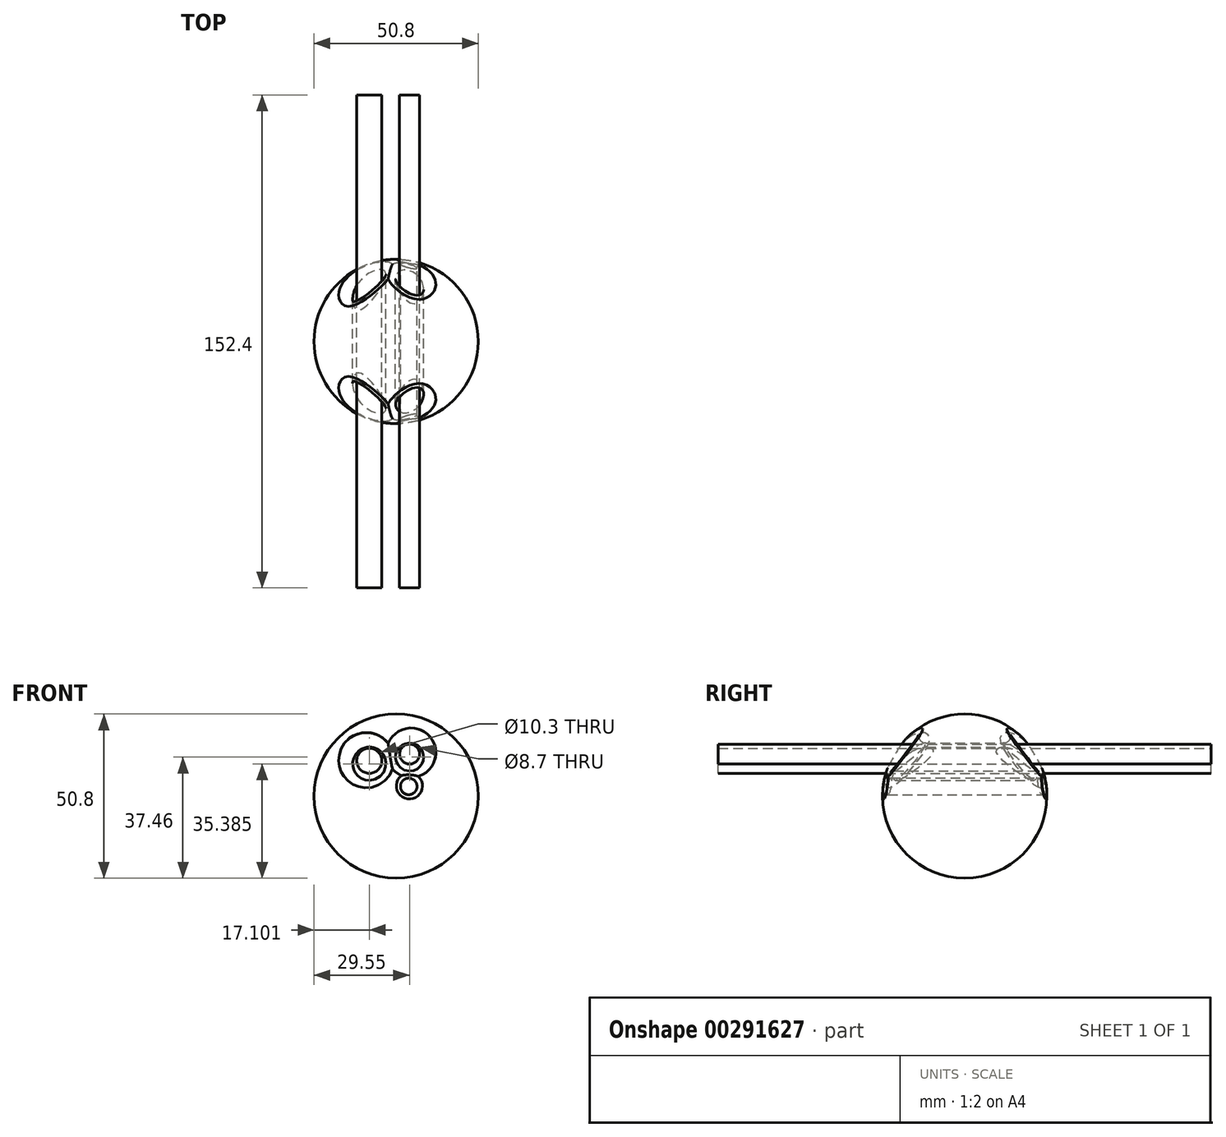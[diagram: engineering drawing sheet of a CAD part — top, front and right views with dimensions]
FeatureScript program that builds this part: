
annotation { "Feature Type Name" : "Feature", "Feature Type Description" : "" }
export const myFeature = defineFeature(function(context is Context, id is Id, definition is map)
    precondition{}
    {
        {
            var Q0;
            Q0=qCreatedBy(makeId("Front.planeOp"),FACE);
            var sketch = newSketch(context, id + "F0", { "sketchPlane" : qUnion([Q0])});
            skCircle(sketch, "E0", {"center": v(0, 0) * mm, "radius": 25.4 * mm});
            skCircle(sketch, "E1", {"center": v(-8.3, 9.99) * mm, "radius": 5.15 * mm});
            skCircle(sketch, "E2", {"center": v(4.15, 12.06) * mm, "radius": 4.35 * mm});
            skCircle(sketch, "E3", {"center": v(3.9, 2.98) * mm, "radius": 2.57 * mm});
            skCircle(sketch, "E4", {"center": v(-8.3, 10.92) * mm, "radius": 3.9 * mm});
            skCircle(sketch, "E5", {"center": v(4.15, 13) * mm, "radius": 3.08 * mm});
            skSolve(sketch);
        }
        {
            var Q0;
            Q0=makeQuery(id+"F0.imprint","IMPRINT",FACE,{"disambiguationData":[TD([[makeQuery(id+"F0.imprint","IMPRINT",EDGE,{"derivedFrom":sQuery(id+"F0.wireOp",EDGE,"E0")}),1.0]])]});
            extrude(context, id + "F1", {"entities" : qUnion([Q0]), "endBound" : BoundingType.SYMMETRIC, "depth" : 50.8 * mm});
        }
        {
            var Q0;
            Q0=makeQuery(id+"F1.opExtrude","CAP_EDGE",EDGE,{"disambiguationData":[OSD([sQuery(id+"F0.wireOp",EDGE,"E0")])],"isStart":false});
            fillet(context, id + "F2", {"entities" : qUnion([Q0]), "radius" : 25.4 * mm, "tangentPropagation" : true, "allowEdgeOverflow" : false});
        }
        {
            var Q0;
            Q0=makeQuery(id+"F1.opExtrude","CAP_EDGE",EDGE,{"disambiguationData":[OSD([sQuery(id+"F0.wireOp",EDGE,"E0")])],"isStart":true});
            fillet(context, id + "F3", {"entities" : qUnion([Q0]), "radius" : 25.4 * mm, "tangentPropagation" : true, "allowEdgeOverflow" : false});
        }
        {
            var Q0;
            Q0=makeQuery(id+"F1.opExtrude","SWEPT_FACE",FACE,{"disambiguationData":[OSD([sQuery(id+"F0.wireOp",EDGE,"E2")])]});
            fillet(context, id + "F4", {"entities" : qUnion([Q0]), "radius" : 2.54 * mm, "tangentPropagation" : true, "allowEdgeOverflow" : false});
        }
        {
            var Q0;
            Q0=makeQuery(id+"F1.opExtrude","SWEPT_FACE",FACE,{"disambiguationData":[OSD([sQuery(id+"F0.wireOp",EDGE,"E1")])]});
            fillet(context, id + "F5", {"entities" : qUnion([Q0]), "radius" : 2.54 * mm, "tangentPropagation" : true, "allowEdgeOverflow" : false});
        }
        {
            var Q0;
            Q0=makeQuery(id+"F1.opExtrude","SWEPT_FACE",FACE,{"disambiguationData":[OSD([sQuery(id+"F0.wireOp",EDGE,"E3")])]});
            fillet(context, id + "F6", {"entities" : qUnion([Q0]), "radius" : 1.27 * mm, "tangentPropagation" : true, "allowEdgeOverflow" : false});
        }
        {
            var Q0;
            Q0=makeQuery(id+"F0.imprint","IMPRINT",FACE,{"disambiguationData":[TD([[makeQuery(id+"F0.imprint","IMPRINT",EDGE,{"derivedFrom":sQuery(id+"F0.wireOp",EDGE,"E4")}),1.0]])]});
            extrude(context, id + "F7", {"entities" : qUnion([Q0]), "endBound" : BoundingType.SYMMETRIC, "depth" : 152.4 * mm});
        }
        {
            var Q0;
            Q0=makeQuery(id+"F0.imprint","IMPRINT",FACE,{"disambiguationData":[TD([[makeQuery(id+"F0.imprint","IMPRINT",EDGE,{"derivedFrom":sQuery(id+"F0.wireOp",EDGE,"E5")}),1.0]])]});
            extrude(context, id + "F8", {"entities" : qUnion([Q0]), "endBound" : BoundingType.SYMMETRIC, "depth" : 152.4 * mm});
        }
    });
